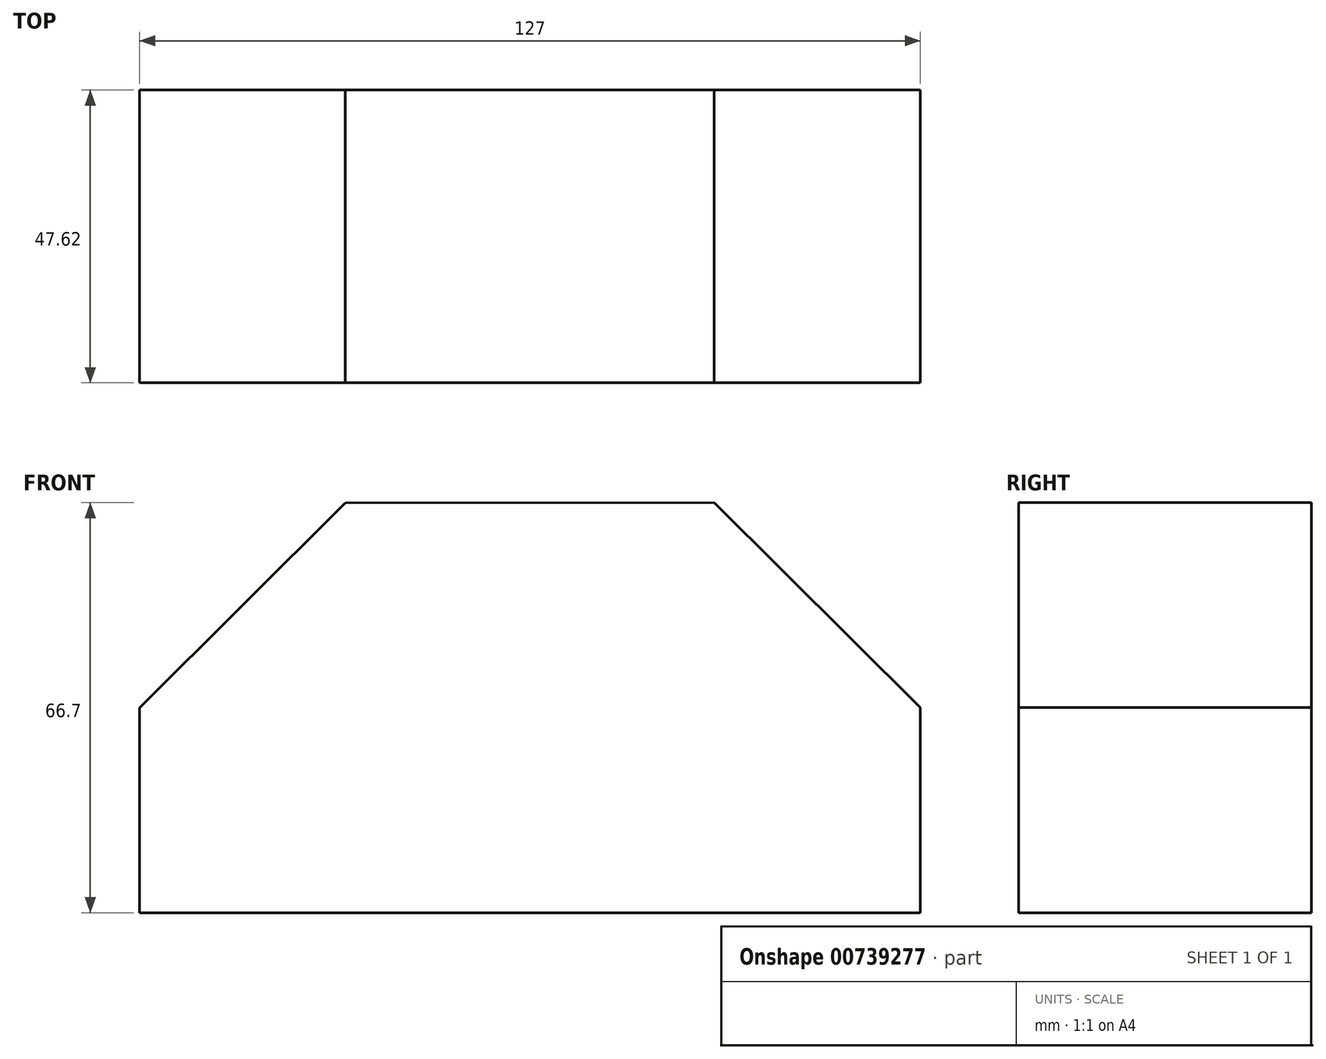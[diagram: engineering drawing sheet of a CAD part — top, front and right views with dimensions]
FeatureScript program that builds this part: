
annotation { "Feature Type Name" : "Feature", "Feature Type Description" : "" }
export const myFeature = defineFeature(function(context is Context, id is Id, definition is map)
    precondition{}
    {
        {
            var Q0;
            Q0=qCreatedBy(makeId("Front.planeOp"),FACE);
            var sketch = newSketch(context, id + "F0", { "sketchPlane" : qUnion([Q0])});
            skLineSegment(sketch, "E0", {"start": v(0, 0) * mm, "end": v(127, 0) * mm});
            skLineSegment(sketch, "E1", {"start": v(127, 0) * mm, "end": v(127, 33.35) * mm});
            skLineSegment(sketch, "E2", {"start": v(0, 0) * mm, "end": v(0, 33.34) * mm});
            skLineSegment(sketch, "E3", {"start": v(33.46, 66.67) * mm, "end": v(93.43, 66.7) * mm});
            skLineSegment(sketch, "E4", {"start": v(-10.04, 0) * mm, "end": v(-10.04, 33.34) * mm});
            skLineSegment(sketch, "E5", {"start": v(0, 33.34) * mm, "end": v(33.46, 66.68) * mm});
            skPoint(sketch, "E6.start.orphan", {"position": v(0, 69.28) * mm});
            skLineSegment(sketch, "E7", {"start": v(127, 33.35) * mm, "end": v(93.43, 66.7) * mm});
            skPoint(sketch, "E8.orphan", {"position": v(127, 66.71) * mm});
            skPoint(sketch, "E9.end.orphan", {"position": v(93.43, 75.29) * mm});
            skPoint(sketch, "E9.start.orphan", {"position": v(127, 67.33) * mm});
            skPoint(sketch, "E10.end.orphan", {"position": v(154.67, 33.35) * mm});
            skPoint(sketch, "E10.start.orphan", {"position": v(154.67, 0) * mm});
            skSolve(sketch);
        }
        {
            var Q0;
            Q0=makeQuery(id+"F0.imprint","IMPRINT",FACE,{"disambiguationData":[TD([[makeQuery(id+"F0.imprint","IMPRINT",EDGE,{"derivedFrom":sQuery(id+"F0.wireOp",EDGE,"E0")}),1.0]])]});
            extrude(context, id + "F1", {"entities" : qUnion([Q0]), "depth" : 47.62 * mm, "offsetDistance" : 25.4 * mm});
        }
    });
